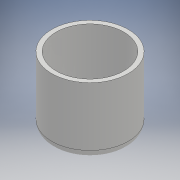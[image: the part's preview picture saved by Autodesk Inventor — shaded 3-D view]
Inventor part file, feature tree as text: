
AUTODESK INVENTOR PART (.ipt)
format: ipt  version: 2017 (Build 210142000, 142)  size: 113,664 bytes
history: native  units: mm
features: extrude x2, sketch x2, fillet x1
ambient origin geometry x8: Origin, YZ Plane, XZ Plane, XY Plane, X Axis, Y Axis, Z Axis, Center Point
bodies: Solid1 (feature_tree)
feature tree (5):
  extrude  "Extrusion1"  Depth=75.0mm
  extrude  "Extrusion2"  Depth=9.0mm
  fillet  "Fillet1"  [1 undecoded]
  sketch  "Sketch1"  dims[d2=75.0mm d3=0.0mm d4=76.0mm]
  sketch  "Sketch2"  dims[d5=71.0mm d6=0.0mm d7=9.0mm]
note: 1 required parameter value undecoded (feature->parameter linkage not recoverable at this tier; creation-order binding heuristic only, values carry confidence <= 0.55)
